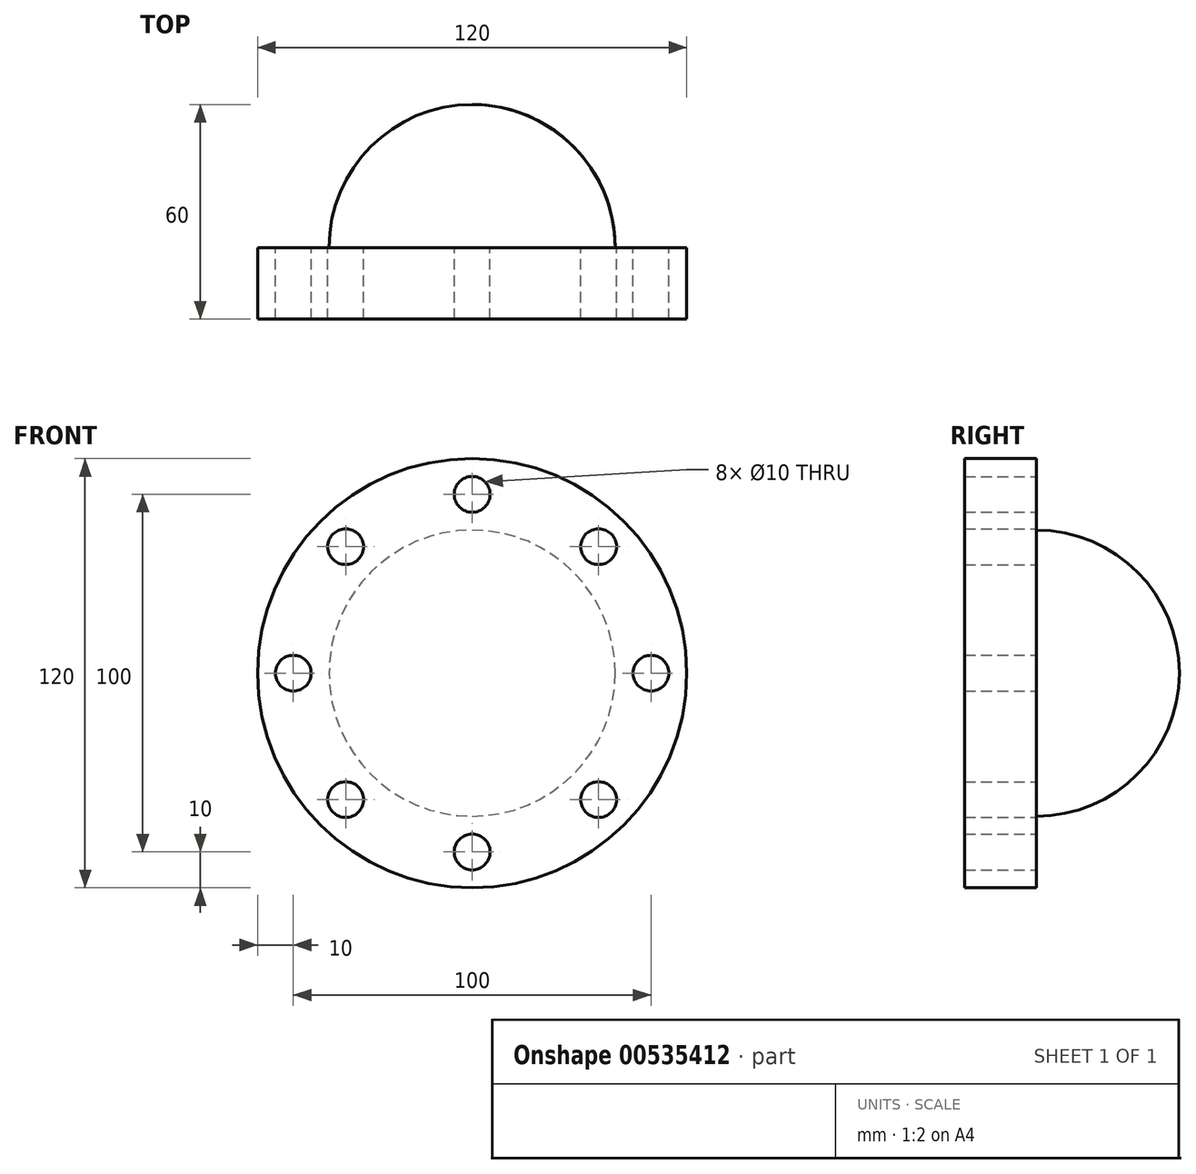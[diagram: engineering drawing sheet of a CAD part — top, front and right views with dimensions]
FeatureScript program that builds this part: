
annotation { "Feature Type Name" : "Feature", "Feature Type Description" : "" }
export const myFeature = defineFeature(function(context is Context, id is Id, definition is map)
    precondition{}
    {
        {
            var Q0;
            Q0=qCreatedBy(makeId("Front.planeOp"),FACE);
            var sketch = newSketch(context, id + "F0", { "sketchPlane" : qUnion([Q0])});
            skCircle(sketch, "E0", {"center": v(0, 0) * mm, "radius": 60 * mm});
            skCircle(sketch, "E1", {"center": v(0, 50) * mm, "radius": 5 * mm});
            skCircle(sketch, "E2.1.0", {"center": v(-35.36, 35.36) * mm, "radius": 5 * mm});
            skCircle(sketch, "E2.2.0", {"center": v(-50, 0) * mm, "radius": 5 * mm});
            skCircle(sketch, "E2.3.0", {"center": v(-35.36, -35.36) * mm, "radius": 5 * mm});
            skCircle(sketch, "E2.4.0", {"center": v(0, -50) * mm, "radius": 5 * mm});
            skCircle(sketch, "E2.5.0", {"center": v(35.36, -35.36) * mm, "radius": 5 * mm});
            skCircle(sketch, "E2.6.0", {"center": v(50, 0) * mm, "radius": 5 * mm});
            skCircle(sketch, "E2.7.0", {"center": v(35.36, 35.36) * mm, "radius": 5 * mm});
            skSolve(sketch);
        }
        {
            var Q0;
            Q0 = qSketchRegion(id + "F0", true);
            extrude(context, id + "F1", {"entities" : qUnion([Q0]), "depth" : 20 * mm, "offsetDistance" : 25.4 * mm});
        }
        {
            var Q0;
            Q0=qCreatedBy(makeId("Top.planeOp"),FACE);
            var sketch = newSketch(context, id + "F2", { "sketchPlane" : qUnion([Q0])});
            skArc(sketch, "E3", {"start": v(40, 0) * mm, "mid": v(28.28, 28.28) * mm, "end": v(0, 40) * mm});
            skLineSegment(sketch, "E4", {"start": v(0, 0) * mm, "end": v(0, 40) * mm});
            skLineSegment(sketch, "E5", {"start": v(0, 0) * mm, "end": v(40, 0) * mm});
            skLineSegment(sketch, "E6", {"start": v(60, 0) * mm, "end": v(60, -20) * mm});
            skLineSegment(sketch, "E7", {"start": v(-60, -20) * mm, "end": v(-60, 0) * mm});
            skSolve(sketch);
        }
        {
            var Q0;
            Q0=makeQuery(id+"F2.imprint","IMPRINT",FACE,{"disambiguationData":[TD([[makeQuery(id+"F2.imprint","IMPRINT",EDGE,{"derivedFrom":sQuery(id+"F2.wireOp",EDGE,"E3")}),1.0]])]});
            var Q1;
            Q1=sQuery(id+"F2.wireOp",EDGE,"E4");
            revolve(context, id + "F3", {"operationType" : NewBodyOperationType.ADD, "entities" : qUnion([Q0]), "axis" : qUnion([Q1]), "revolveType" : RevolveType.FULL});
        }
    });
